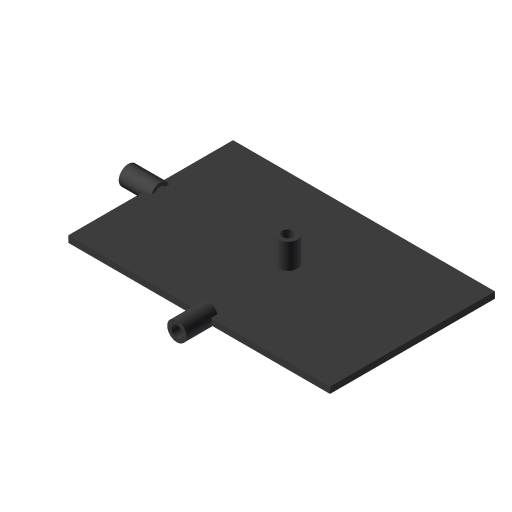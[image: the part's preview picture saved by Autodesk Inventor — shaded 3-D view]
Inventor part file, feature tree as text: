
AUTODESK INVENTOR PART (.ipt)
format: ipt  version: 2023.4 (Build 274418000, 418)  size: 172,544 bytes
history: native  units: in
note: dims shown in document units (in); Inventor stores cm internally (conversion verified against a paired STEP export)
features: extrude x4, sketch x4
ambient origin geometry x8: Origin, YZ Plane, XZ Plane, XY Plane, X Axis, Y Axis, Z Axis, Center Point
bodies: Solid1 (feature_tree)
feature tree (8):
  extrude  "Extrusion1"  Depth=8.0709in
  extrude  "Extrusion2"  TaperAngle=0.0deg  [1 undecoded]
  extrude  "Extrusion3"  TaperAngle=0.0deg  [1 undecoded]
  extrude  "Extrusion4"  Depth=0.7874in TaperAngle=0.0deg
  sketch  "Sketch1"  dims[d0=5.0787in d1=8.0709in]
  sketch  "Sketch2"  dims[d2=0.0in d3=0.0in]
  sketch  "Sketch3"  dims[d10=0.1969in d11=0.0in]
  sketch  "Sketch4"  dims[d18=0.3543in d19=0.4724in d20=0.5906in d21=0.185in d22=0.0394in d23=0.0394in d26=0.0in d28=0.7874in d29=0.0in d30=0.3543in d31=0.4724in d32=0.5906in d33=0.185in d34=0.0394in d35=0.0394in d36=0.0in d37=4.1339in d38=0.0in d40=2.6378in d41=4.1339in d42=0.7874in d43=0.1969in d44=0.0in d45=0.0in d46=0.3543in d47=0.4724in d48=0.5906in d49=0.185in d50=0.0394in d51=0.0394in d52=0.0in d53=0.0in d54=2.6378in d55=0.7874in d56=0.1969in d57=0.0in d58=0.0in]
note: 2 required parameter values undecoded (feature->parameter linkage not recoverable at this tier; creation-order binding heuristic only, values carry confidence <= 0.55)
